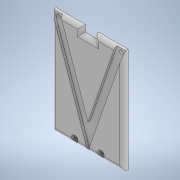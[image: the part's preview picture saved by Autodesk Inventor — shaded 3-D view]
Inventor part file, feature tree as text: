
AUTODESK INVENTOR PART (.ipt)
format: ipt  version: 2022 (Build 260153000, 153)  size: 215,552 bytes
history: native  units: in
note: dims shown in document units (in); Inventor stores cm internally (conversion verified against a paired STEP export)
features: projected_geometry x7, extrude x4, sketch x4, fillet x1
ambient origin geometry x8: Origin, YZ Plane, XZ Plane, XY Plane, X Axis, Y Axis, Z Axis, Center Point
bodies: Solid1 (feature_tree)
feature tree (16):
  extrude  "Extrusion1"  Depth=3.0in
  extrude  "Extrusion2"  Depth=0.141in
  fillet  "Fillet1"  Radius=0.4in
  extrude  "Extrusion3"  Depth=0.12in
  extrude  "Extrusion4"  Depth=0.2in
  sketch  "Sketch1"  dims[d0=2.2in d1=3.0in]
  sketch  "Sketch2"  dims[d2=0.2in d3=0.141in d4=0.4in]
  projected_geometry  "Projected Loop1"
  sketch  "Sketch3"  dims[d5=0.8in d6=0.12in]
  projected_geometry  "Projected Loop2"
  projected_geometry  "Projected Loop3"
  projected_geometry  "Projected Loop4"
  projected_geometry  "Projected Loop5"
  sketch  "Sketch4"  dims[d7=0.12in d8=0.2in d9=0.125in d10=0.0in d12=0.0625in d13=0.0in d14=0.125in d15=0.01in d16=0.12in d17=0.125in d19=1.0in d20=0.0in d21=2.934in d22=0.5558in d23=0.1969in d24=0.1969in d25=0.0625in d26=0.0in]
  projected_geometry  "Projected Loop6"
  projected_geometry  "Projected Loop7"
